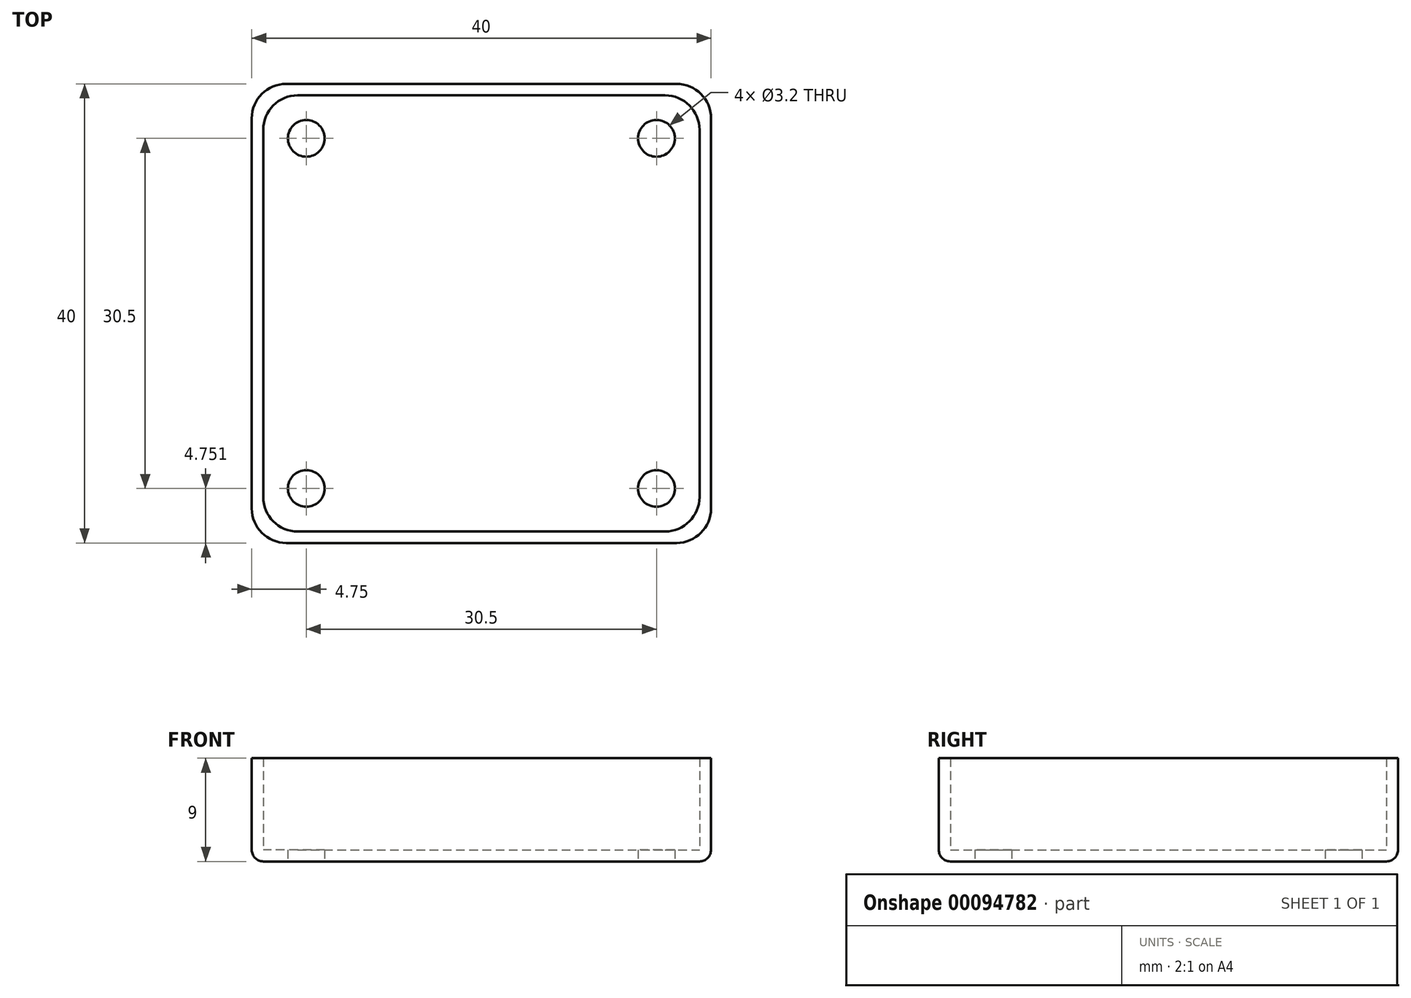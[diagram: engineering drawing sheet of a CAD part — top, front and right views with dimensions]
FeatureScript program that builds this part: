
annotation { "Feature Type Name" : "Feature", "Feature Type Description" : "" }
export const myFeature = defineFeature(function(context is Context, id is Id, definition is map)
    precondition{}
    {
        {
            var Q0;
            Q0=qCreatedBy(makeId("Top.planeOp"),FACE);
            var sketch = newSketch(context, id + "F0", { "sketchPlane" : qUnion([Q0])});
            skLineSegment(sketch, "E0.bottom", {"start": v(-21.32, 19.67) * mm, "end": v(18.68, 19.67) * mm});
            skLineSegment(sketch, "E0.top", {"start": v(-21.32, -20.33) * mm, "end": v(18.68, -20.33) * mm});
            skLineSegment(sketch, "E0.left", {"start": v(-21.32, 19.67) * mm, "end": v(-21.32, -20.33) * mm});
            skLineSegment(sketch, "E0.right", {"start": v(18.68, 19.67) * mm, "end": v(18.68, -20.33) * mm});
            skCircle(sketch, "E1", {"center": v(-16.57, -15.58) * mm, "radius": 1.6 * mm});
            skCircle(sketch, "E2", {"center": v(13.93, -15.58) * mm, "radius": 1.6 * mm});
            skCircle(sketch, "E3", {"center": v(13.93, 14.92) * mm, "radius": 1.6 * mm});
            skCircle(sketch, "E4", {"center": v(-16.57, 14.92) * mm, "radius": 1.6 * mm});
            skPoint(sketch, "E5.end.orphan", {"position": v(-1.32, 14.92) * mm});
            skPoint(sketch, "E6.start.orphan", {"position": v(-1.32, 19.67) * mm});
            skPoint(sketch, "E7.orphan", {"position": v(-21.32, -0.33) * mm});
            skPoint(sketch, "E8.end.orphan", {"position": v(18.68, -0.33) * mm});
            skPoint(sketch, "E9.start.orphan", {"position": v(-1.32, -0.33) * mm});
            skPoint(sketch, "E10.trimOffspring.end.orphan", {"position": v(-1.32, -20.33) * mm});
            skPoint(sketch, "E11.start.orphan", {"position": v(-1.32, -15.58) * mm});
            skSolve(sketch);
        }
        {
            var Q0;
            Q0=makeQuery(id+"F0.imprint","IMPRINT",FACE,{"disambiguationData":[TD([[makeQuery(id+"F0.imprint","IMPRINT",EDGE,{"derivedFrom":sQuery(id+"F0.wireOp",EDGE,"E0.bottom")}),-1.0]])]});
            extrude(context, id + "F1", {"entities" : qUnion([Q0]), "depth" : 1 * mm});
        }
        {
            var Q0;
            Q0=makeQuery(id+"F1.opExtrude","CAP_FACE",FACE,{"disambiguationData":[OSD([sQuery(id+"F0.wireOp",EDGE,"E0.bottom"),sQuery(id+"F0.wireOp",EDGE,"E0.top"),sQuery(id+"F0.wireOp",EDGE,"E0.left"),sQuery(id+"F0.wireOp",EDGE,"E0.right"),sQuery(id+"F0.wireOp",EDGE,"E1"),sQuery(id+"F0.wireOp",EDGE,"E2"),sQuery(id+"F0.wireOp",EDGE,"E3"),sQuery(id+"F0.wireOp",EDGE,"E4")])],"isStart":false});
            var sketch = newSketch(context, id + "F2", { "sketchPlane" : qUnion([Q0])});
            skLineSegment(sketch, "E12.0", {"start": v(18.68, 14.67) * mm, "end": v(18.68, -15.33) * mm});
            skLineSegment(sketch, "E13.0", {"start": v(-16.32, 19.67) * mm, "end": v(13.68, 19.67) * mm});
            skLineSegment(sketch, "E14.0", {"start": v(-21.32, 14.67) * mm, "end": v(-21.32, -15.33) * mm});
            skLineSegment(sketch, "E15.0", {"start": v(-16.32, -20.33) * mm, "end": v(13.68, -20.33) * mm});
            skLineSegment(sketch, "E16", {"start": v(17.68, 14.67) * mm, "end": v(17.68, -15.33) * mm});
            skLineSegment(sketch, "E17", {"start": v(13.68, 18.67) * mm, "end": v(-16.32, 18.67) * mm});
            skLineSegment(sketch, "E18", {"start": v(-20.32, 14.67) * mm, "end": v(-20.32, -15.33) * mm});
            skLineSegment(sketch, "E19", {"start": v(-16.32, -19.33) * mm, "end": v(13.68, -19.33) * mm});
            skLineSegment(sketch, "E20", {"start": v(-16.32, 18.67) * mm, "end": v(-20.32, 18.67) * mm});
            skLineSegment(sketch, "E21", {"start": v(-20.32, 14.67) * mm, "end": v(-20.32, 18.67) * mm});
            skLineSegment(sketch, "E22", {"start": v(13.68, 18.67) * mm, "end": v(17.68, 18.67) * mm});
            skLineSegment(sketch, "E23", {"start": v(17.68, 14.67) * mm, "end": v(17.68, 18.67) * mm});
            skLineSegment(sketch, "E24", {"start": v(17.68, -15.33) * mm, "end": v(17.68, -19.33) * mm});
            skLineSegment(sketch, "E25", {"start": v(13.68, -19.33) * mm, "end": v(17.68, -19.33) * mm});
            skLineSegment(sketch, "E26", {"start": v(-16.32, -19.33) * mm, "end": v(-20.32, -19.33) * mm});
            skLineSegment(sketch, "E27", {"start": v(-20.32, -15.33) * mm, "end": v(-20.32, -19.33) * mm});
            skSolve(sketch);
        }
        {
            var Q0;
            {var subQ8=sQuery(id+"F2.wireOp",EDGE,"E12.0");Q0=makeQuery(id+"F2.imprint","IMPRINT",FACE,{"disambiguationData":[TD([[makeQuery(id+"F2.imprint","IMPRINT",EDGE,{"derivedFrom":subQ8}),-1.0]])]});}
            extrude(context, id + "F3", {"entities" : qUnion([Q0]), "operationType" : NewBodyOperationType.ADD, "depth" : 8 * mm});
        }
        {
            var Q0;
            Q0=makeQuery(id+"F3.opExtrude","SWEPT_EDGE",EDGE,{"disambiguationData":[OSD([sQuery(id+"F2.wireOp",EDGE,"E26"),sQuery(id+"F2.wireOp",EDGE,"E27")])]});
            var Q1;
            Q1=makeQuery(id+"F3.opExtrude","SWEPT_EDGE",EDGE,{"disambiguationData":[OSD([sQuery(id+"F2.wireOp",EDGE,"E20"),sQuery(id+"F2.wireOp",EDGE,"E21")])]});
            var Q2;
            Q2=makeQuery(id+"F3.opExtrude","SWEPT_EDGE",EDGE,{"disambiguationData":[OSD([sQuery(id+"F2.wireOp",EDGE,"E22"),sQuery(id+"F2.wireOp",EDGE,"E23")])]});
            var Q3;
            Q3=makeQuery(id+"F3.opExtrude","SWEPT_EDGE",EDGE,{"disambiguationData":[OSD([sQuery(id+"F2.wireOp",EDGE,"E24"),sQuery(id+"F2.wireOp",EDGE,"E25")])]});
            var Q4;
            {var subQ0=sQuery(id+"F0.wireOp",EDGE,"E0.right");var subQ1=sQuery(id+"F0.wireOp",EDGE,"E0.top");Q4=makeQuery(id+"F3.boolean.opBoolean","MERGE",EDGE,{"derivedFrom":[makeQuery(id+"F1.opExtrude","SWEPT_EDGE",EDGE,{"disambiguationData":[OSD([subQ1,subQ0])]}),makeQuery(id+"F3.opExtrude","SWEPT_EDGE",EDGE,{"disambiguationData":[OSD([subQ1,subQ0])]})]});}
            var Q5;
            {var subQ0=sQuery(id+"F0.wireOp",EDGE,"E0.right");var subQ1=sQuery(id+"F0.wireOp",EDGE,"E0.bottom");Q5=makeQuery(id+"F3.boolean.opBoolean","MERGE",EDGE,{"derivedFrom":[makeQuery(id+"F1.opExtrude","SWEPT_EDGE",EDGE,{"disambiguationData":[OSD([subQ1,subQ0])]}),makeQuery(id+"F3.opExtrude","SWEPT_EDGE",EDGE,{"disambiguationData":[OSD([subQ1,subQ0])]})]});}
            var Q6;
            {var subQ0=sQuery(id+"F0.wireOp",EDGE,"E0.left");var subQ1=sQuery(id+"F0.wireOp",EDGE,"E0.bottom");Q6=makeQuery(id+"F3.boolean.opBoolean","MERGE",EDGE,{"derivedFrom":[makeQuery(id+"F1.opExtrude","SWEPT_EDGE",EDGE,{"disambiguationData":[OSD([subQ1,subQ0])]}),makeQuery(id+"F3.opExtrude","SWEPT_EDGE",EDGE,{"disambiguationData":[OSD([subQ1,subQ0])]})]});}
            var Q7;
            {var subQ0=sQuery(id+"F0.wireOp",EDGE,"E0.left");var subQ1=sQuery(id+"F0.wireOp",EDGE,"E0.top");Q7=makeQuery(id+"F3.boolean.opBoolean","MERGE",EDGE,{"derivedFrom":[makeQuery(id+"F1.opExtrude","SWEPT_EDGE",EDGE,{"disambiguationData":[OSD([subQ1,subQ0])]}),makeQuery(id+"F3.opExtrude","SWEPT_EDGE",EDGE,{"disambiguationData":[OSD([subQ1,subQ0])]})]});}
            fillet(context, id + "F4", {"entities" : qUnion([Q0, Q1, Q2, Q3, Q4, Q5, Q6, Q7]), "radius" : 3 * mm, "tangentPropagation" : true, "allowEdgeOverflow" : false});
        }
        {
            var Q0;
            Q0=makeQuery(id+"F1.opExtrude","CAP_EDGE",EDGE,{"disambiguationData":[OSD([sQuery(id+"F0.wireOp",EDGE,"E0.bottom")])],"isStart":true});
            fillet(context, id + "F5", {"entities" : qUnion([Q0]), "radius" : 1 * mm, "tangentPropagation" : true, "allowEdgeOverflow" : false});
        }
    });
